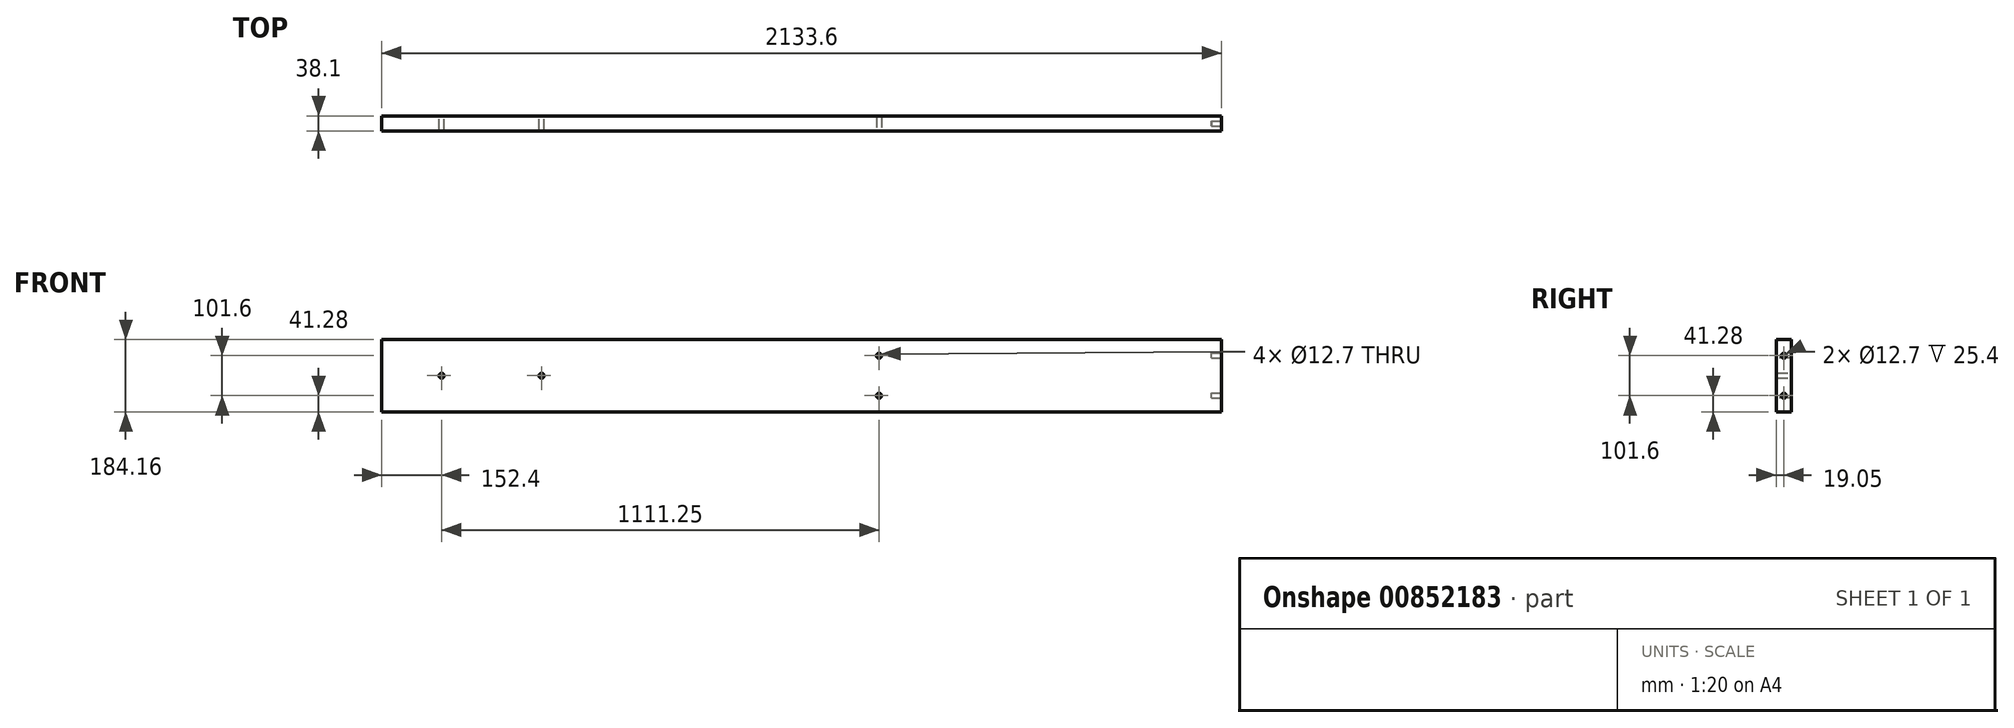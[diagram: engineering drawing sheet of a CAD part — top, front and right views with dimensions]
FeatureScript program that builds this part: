
annotation { "Feature Type Name" : "Feature", "Feature Type Description" : "" }
export const myFeature = defineFeature(function(context is Context, id is Id, definition is map)
    precondition{}
    {
        {
            var Q0;
            Q0=qCreatedBy(makeId("Front.planeOp"),FACE);
            var sketch = newSketch(context, id + "F0", { "sketchPlane" : qUnion([Q0])});
            skLineSegment(sketch, "E0.bottom", {"start": v(1066.8, -92.08) * mm, "end": v(-1066.8, -92.08) * mm});
            skLineSegment(sketch, "E0.top", {"start": v(1066.8, 92.08) * mm, "end": v(-1066.8, 92.07) * mm});
            skLineSegment(sketch, "E0.left", {"start": v(1066.8, -92.08) * mm, "end": v(1066.8, 92.07) * mm});
            skLineSegment(sketch, "E0.right", {"start": v(-1066.8, -92.08) * mm, "end": v(-1066.8, 92.07) * mm});
            skPoint(sketch, "E0.middle", {"position": v(0, 0) * mm});
            skSolve(sketch);
        }
        {
            var Q0;
            Q0=qSketchRegion(id+"F0",true);
            extrude(context, id + "F1", {"entities" : qUnion([Q0]), "endBound" : BoundingType.SYMMETRIC, "depth" : 38.1 * mm, "offsetDistance" : 25.4 * mm});
        }
        {
            var Q0;
            Q0=makeQuery(id+"F1.opExtrude","SWEPT_FACE",FACE,{"disambiguationData":[OSD([sQuery(id+"F0.wireOp",EDGE,"E0.left")])]});
            var sketch = newSketch(context, id + "F2", { "sketchPlane" : qUnion([Q0])});
            skLineSegment(sketch, "E1", {"start": v(0, 50.8) * mm, "end": v(0, -50.8) * mm, "construction": true});
            skCircle(sketch, "E2", {"center": v(0, 50.8) * mm, "radius": 6.35 * mm});
            skCircle(sketch, "E3", {"center": v(0, -50.8) * mm, "radius": 6.35 * mm});
            skSolve(sketch);
        }
        {
            var Q0;
            Q0 = qSketchRegion(id + "F2", true);
            extrude(context, id + "F3", {"entities" : qUnion([Q0]), "operationType" : NewBodyOperationType.REMOVE, "oppositeDirection" : true, "depth" : 25.4 * mm, "offsetDistance" : 25.4 * mm});
        }
        {
            var Q0;
            Q0=makeQuery(id+"F1.opExtrude","CAP_FACE",FACE,{"disambiguationData":[OSD([sQuery(id+"F0.wireOp",EDGE,"E0.bottom"),sQuery(id+"F0.wireOp",EDGE,"E0.top"),sQuery(id+"F0.wireOp",EDGE,"E0.left"),sQuery(id+"F0.wireOp",EDGE,"E0.right")])],"isStart":false});
            var sketch = newSketch(context, id + "F4", { "sketchPlane" : qUnion([Q0])});
            skLineSegment(sketch, "E4", {"start": v(196.85, 50.8) * mm, "end": v(196.85, -50.8) * mm, "construction": true});
            skCircle(sketch, "E5", {"center": v(196.85, 50.8) * mm, "radius": 6.35 * mm});
            skCircle(sketch, "E6", {"center": v(196.85, -50.8) * mm, "radius": 6.35 * mm});
            skLineSegment(sketch, "E7", {"start": v(0, 0) * mm, "end": v(1066.8, 0) * mm, "construction": true});
            skSolve(sketch);
        }
        {
            var Q0;
            Q0 = qSketchRegion(id + "F4", true);
            extrude(context, id + "F5", {"entities" : qUnion([Q0]), "operationType" : NewBodyOperationType.REMOVE, "oppositeDirection" : true, "depth" : 50.8 * mm, "offsetDistance" : 25.4 * mm});
        }
        {
            var Q0;
            Q0=qCreatedBy(makeId("Front.planeOp"),FACE);
            var sketch = newSketch(context, id + "F6", { "sketchPlane" : qUnion([Q0])});
            skLineSegment(sketch, "E8", {"start": v(0, 0) * mm, "end": v(-1079.54, 0) * mm, "construction": true});
            skCircle(sketch, "E9", {"center": v(-914.4, 0) * mm, "radius": 6.35 * mm});
            skCircle(sketch, "E10", {"center": v(-660.4, 0) * mm, "radius": 6.35 * mm});
            skSolve(sketch);
        }
        {
            var Q0;
            Q0 = qSketchRegion(id + "F6", true);
            extrude(context, id + "F7", {"entities" : qUnion([Q0]), "operationType" : NewBodyOperationType.REMOVE, "endBound" : BoundingType.SYMMETRIC, "depth" : 50.8 * mm, "offsetDistance" : 25.4 * mm});
        }
    });
